# Revit family: B200S-LF-WH.BIM
name_source: partatom
category: Fire Alarm Devices
units: mm (PartAtom-declared; Revit-internal decimal feet)

## family parameters
Cut with Voids When Loaded = No
Host = Face
Maintain Annotation Orientation = Yes
OmniClass Number = 23.85.30.21
OmniClass Title = Environmental Detection/Registration
Part Type = Normal
Room Calculation Point = No
Round Connector Dimension = Use Diameter
Shared = No

## types (10) — shared parameters
Agency Listing = UL
Assembly Code = D5030700
Default Elevation = 6' - 8"
Detector Type = P-CO
Main Electrical Connection = Signaling Line Circuit
Manufacturer = Fire Lite
Mounting Requirements = Standard 4 inch square, 4 inch octagonal, or single gang electrical box.
URL = www.firelite.com

## per-type parameters (varying)
| type | Base Label | Base Select | Base Thickness | Description | Diameter | Finish | Height | Model | Puck Base | Specality Base | Standard Base |
| Detector_with_Flanged_Base_White |  | DetectorBase-Select_Series : Flanged Base | 0' - 0 7/8" | Intelligent Plug-In Photo-CO Detector / Flanged Mounting Base | 0' - 6" | Plastic_FireLite_White | 0' - 1 11/16" | SD365CO/B300-6 | No | No | Yes |
| Detector_with_Flanged_Base_Black |  | DetectorBase-Select_Series : Flanged Base | 0' - 0 7/8" | Intelligent Plug-In Photo-CO Detector / Flanged Mounting Base/Color Kit | 0' - 6" | Plastic_FireLite_Black | 0' - 1 11/16" | SD365CO/B300-6/CK300-BL | No | No | Yes |
| Detector_with_Isolator_Base_White | IB | DetectorBase-Select_Series : Speciality Base | 0' - 1 11/16" | Intelligent Plug-In Photo-CO Detector / Isolator Base | 0' - 6 7/8" | Plastic_FireLite_White | 0' - 2 9/16" | SD365CO/B224BI | No | Yes | No |
| Detector_with_Puck_Base_White | 4" | DetectorBase-Select_Series : Puck Base | 0' - 0 7/8" | Intelligent Plug-In Photo-CO Detector / 4" Mounting Base | 0' - 4" | Plastic_FireLite_White | 0' - 1 11/16" | SD365CO/B501 | Yes | No | No |
| Detector_with_Puck_Base_Black | 4" | DetectorBase-Select_Series : Puck Base | 0' - 0 7/8" | Intelligent Plug-In Photo-CO Detector / 4" Mounting Base/Color Kit | 0' - 4" | Plastic_FireLite_Black | 0' - 1 11/16" | SD365CO/B501-BL/CK300-BL | Yes | No | No |
| Detector_with_Relay_Base_White | RB | DetectorBase-Select_Series : Speciality Base | 0' - 1 11/16" | Intelligent Plug-In Photo-CO Detector / Relay Base | 0' - 6 7/8" | Plastic_FireLite_White | 0' - 2 9/16" | SD365CO/B224RB | No | Yes | No |
| Detector_with_Sounder_Base_White | SB | DetectorBase-Select_Series : Speciality Base | 0' - 1 11/16" | Intelligent Plug-In Photo-CO Detector / Sounder Base | 0' - 6 7/8" | Plastic_FireLite_White | 0' - 2 9/16" | SD365CO/B200SR | No | Yes | No |
| Detector_with_Low_Freq_Sounder_Base_White | LF | DetectorBase-Select_Series : Speciality Base | 0' - 1 11/16" | Intelligent Plug-In Photo-CO Detector / Low Freq Sounder Base | 0' - 6 7/8" | Plastic_FireLite_White | 0' - 2 9/16" | SD365CO/B200SR-LF | No | Yes | No |
| Detector_with_Sync_Sounder_Base_White | SB | DetectorBase-Select_Series : Speciality Base | 0' - 1 11/16" | Intelligent Plug-In Photo-CO Detector / Sounder Base | 0' - 6 7/8" | Plastic_FireLite_White | 0' - 2 9/16" | SD365CO/B200S | No | Yes | No |
| Detector_with_Low_Freq_Sync_Sounder_Base_White | LF | DetectorBase-Select_Series : Speciality Base | 0' - 1 11/16" | Intelligent Plug-In Photo-CO Detector / Low Freq Sounder Base | 0' - 6 7/8" | Plastic_FireLite_White | 0' - 2 9/16" | B200S-LF-WH | No | Yes | No |

## geometry (parser evidence)
native form markers: Sweep x9
no freeform markers — native parametric forms only
